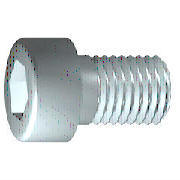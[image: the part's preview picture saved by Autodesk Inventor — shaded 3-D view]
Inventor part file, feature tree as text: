
AUTODESK INVENTOR PART (.ipt)
format: ipt  version: 2019 (Build 230136000, 136)  size: 193,536 bytes
history: native  units: mm (DEFAULTED — no unit token found)
features: sketch x2, extrude x1, plane x1, fillet x1
ambient origin geometry x7: Origin, YZ Plane, XY Plane, X Axis, Y Axis, Z Axis, Center Point
bodies: Solid1 (feature_tree), Body (feature_tree)
feature tree (5):
  extrude  "Slot"  Depth=3.0mm
  plane  "Work Plane1"
  fillet  "Fillet2"  Radius=3.0mm
  sketch  "Sketch1"  dims[d1=4.5mm d2=0.306825mm d3=3.0mm]
  sketch  "Sketch2"  dims[d4=1.3mm d5=60.0deg d6=3.0mm d7=3.0mm d8=2.886751mm d9=5.5mm d10=90.0deg d11=10.0mm d12=0.0mm d13=4.5mm d14=0.0mm d15=0.306725mm d16=0.306725mm d17=0.3mm d19=0.0mm d26=6.0mm d27=45.0deg d28=0.0mm d29=0.0mm d30=0.1mm]
